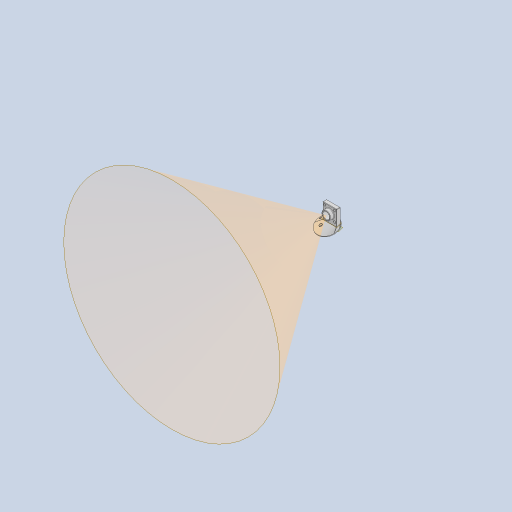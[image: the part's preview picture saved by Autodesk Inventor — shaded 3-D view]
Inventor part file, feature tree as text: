
AUTODESK INVENTOR PART (.ipt)
format: ipt  version: 2023.4 (Build 274418000, 418)  size: 450,560 bytes
history: native  units: in
note: dims shown in document units (in); Inventor stores cm internally (conversion verified against a paired STEP export)
features: extrude x7, hole x3, fillet x3, other x3, projected_geometry x3, plane x2, chamfer x2, loft x1, sketch x1, revolve x1
ambient origin geometry x8: Origin, YZ Plane, XZ Plane, XY Plane, X Axis, Y Axis, Z Axis, Center Point
bodies: Solid1 (feature_tree)
feature tree (26):
  extrude  "Extrusion1"  Depth=0.15in
  extrude  "Extrusion2"  Depth=0.15in TaperAngle=0.0deg
  plane  "Work Plane1"
  extrude  "Extrusion3"  Depth=0.15in
  loft  "Loft1"
  extrude  "Extrusion4"  Depth=0.15in
  hole  "Hole1"  [1 undecoded]
  extrude  "Extrusion5"  Depth=0.15in TaperAngle=0.0deg
  extrude  "Extrusion6"  TaperAngle=0.0deg  [1 undecoded]
  hole  "Hole2"  [1 undecoded]
  plane  "Work Plane2"
  hole  "Hole3"  [1 undecoded]
  fillet  "Fillet1"  Radius=0.3in
  chamfer  "Chamfer1"  Distance=1.1875in
  fillet  "Fillet2"  Radius=0.5in
  extrude  "Extrusion7"  Depth=0.15in
  fillet  "Fillet3"  Radius=1.3386in
  chamfer  "Chamfer2"  Distance=0.15in
  other  "Edges1"
  other  "Edges2"
  projected_geometry  "Projected Loop1"
  projected_geometry  "Projected Loop2"
  sketch  "Sketch11"  dims[d0=1.875in d1=0.525in d2=1.875in d3=0.0in d4=0.481in d5=1.875in d6=0.0in d7=0.6in d9=2.75in d10=0.1in d11=0.0in d12=0.0in d13=90.0deg d14=0.0in d15=90.0deg d16=1.6in d17=0.3in d18=0.0in d19=0.9in d20=0.75in d21=0.119in d22=0.25in d23=0.6871in d24=1.0in d25=0.8108in d26=1.1875in d27=0.5in d28=0.0in d29=0.1839in d30=1.3386in d31=0.15in d32=0.0in d33=0.094in d34=0.75in d35=0.251in d36=0.15in d37=0.6871in d38=1.0in d39=0.8108in d40=0.9792in d41=0.9792in d42=315.0deg d45=0.177in d46=0.75in d47=0.313in d48=0.45in d49=0.5635in d50=1.0in d51=0.8108in d52=0.05in d53=0.05in d54=0.125in d55=45.0deg d56=0.0625in d57=1.0in d58=1.0in d59=0.0in d60=0.25in d61=0.0312in d62=0.125in d63=45.0deg d64=0.2405in d65=90.0deg]
  other  "Srf1"
  revolve  "RevolutionSrf1"  [1 undecoded]
  projected_geometry  "Project Cut Edges1"
note: 5 required parameter values undecoded (feature->parameter linkage not recoverable at this tier; creation-order binding heuristic only, values carry confidence <= 0.55)